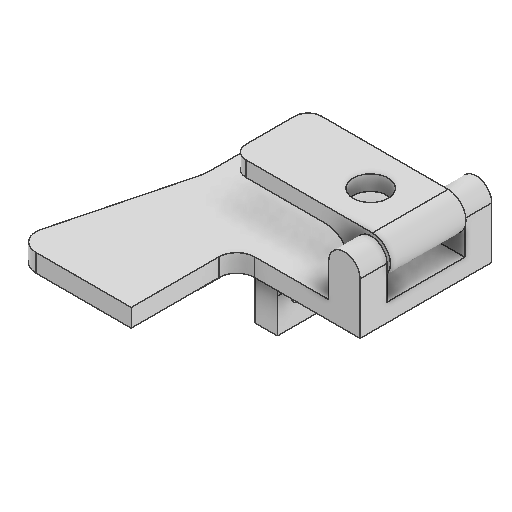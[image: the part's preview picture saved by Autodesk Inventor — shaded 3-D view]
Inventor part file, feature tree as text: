
AUTODESK INVENTOR PART (.ipt)
format: ipt  version: 2025 (Build 290162000, 162)  size: 641,024 bytes
history: native  units: mm
features: projected_geometry x27, sketch x26, extrude x24, fillet x9, plane x7, mirror x3, helix x1
ambient origin geometry x8: Origin, YZ Plane, XZ Plane, XY Plane, X Axis, Y Axis, Z Axis, Center Point
bodies: Solid1 (feature_tree)
feature tree (97):
  extrude  "Extrusion1"  Depth=152.4mm
  plane  "Work Plane1"
  extrude  "Extrusion2"  [1 undecoded]
  extrude  "Extrusion3"  Depth=0.25mm
  extrude  "Extrusion4"  Depth=25.4mm
  fillet  "Fillet1"  Radius=2.75mm
  extrude  "Extrusion5"  Depth=10.0mm TaperAngle=0.0deg
  extrude  "Extrusion6"  Depth=10.0mm
  extrude  "Extrusion7"  Depth=8.0mm TaperAngle=0.0deg
  extrude  "Extrusion8"  Depth=10.0mm TaperAngle=0.0deg
  extrude  "Extrusion9"  Depth=25.4mm TaperAngle=0.0deg
  extrude  "Extrusion10"  Depth=14.0mm
  extrude  "Extrusion11"  Depth=8.0mm
  plane  "Work Plane2"
  extrude  "Extrusion12"  Depth=15.0mm
  mirror  "Mirror1"
  plane  "Work Plane3"
  sketch  "Sketch13"  dims[d37=0.5mm d38=0.5mm]
  plane  "Work Plane4"
  extrude  "Extrusion13"  Depth=0.5mm
  extrude  "Extrusion14"  Depth=0.5mm
  fillet  "Fillet2"  Radius=55.0mm
  fillet  "Fillet3"  [1 undecoded]
  extrude  "Extrusion15"  Depth=10.0mm
  extrude  "Extrusion16"  TaperAngle=0.0deg  [1 undecoded]
  fillet  "Fillet5"  Radius=1.5mm
  extrude  "Extrusion17"  Depth=6.0mm
  extrude  "Extrusion18"  Depth=20.0mm TaperAngle=0.0deg
  fillet  "Fillet6"  Radius=6.0mm
  fillet  "Fillet7"  Radius=6.0mm
  plane  "Work Plane5"
  helix  "Coil2"  [1 undecoded]
  plane  "Work Plane6"
  extrude  "Extrusion19"  Depth=10.0mm
  fillet  "Fillet8"  Radius=2.5mm
  sketch  "Sketch21"  dims[d86=2.0mm d87=0.0mm d88=0.0mm]
  sketch  "Sketch22"  dims[d89=8.0mm d90=0.0mm d91=45.4mm]
  extrude  "Extrusion20"  TaperAngle=0.0deg  [1 undecoded]
  extrude  "Extrusion21"  TaperAngle=0.0deg  [1 undecoded]
  extrude  "Extrusion22"  Depth=45.4mm
  extrude  "Extrusion23"  Depth=10.0mm
  extrude  "Extrusion24"  Depth=50.8mm
  plane  "Work Plane7"
  mirror  "Mirror2"
  fillet  "Fillet9"  Radius=30.0mm
  fillet  "Fillet10"  Radius=2.6mm
  mirror  "Mirror3"
  sketch  "Sketch1"  dims[d0=25.4mm d1=152.4mm]
  sketch  "Sketch2"  dims[d2=10.0mm d3=0.0mm d4=-50.8mm]
  projected_geometry  "Projected Loop1"
  sketch  "Sketch3"  dims[d5=25.4mm d6=0.25mm]
  projected_geometry  "Projected Loop2"
  sketch  "Sketch4"  dims[d7=50.8mm d8=0.0mm d9=25.4mm d10=2.75mm]
  sketch  "Sketch5"  dims[d11=35.45mm d12=0.0mm d13=10.0mm d14=0.0mm]
  projected_geometry  "Projected Loop3"
  sketch  "Sketch6"  dims[d15=10.0mm d16=55.0mm]
  projected_geometry  "Projected Loop4"
  sketch  "Sketch7"  dims[d17=55.0mm d18=8.0mm d19=0.0mm]
  projected_geometry  "Projected Loop5"
  sketch  "Sketch8"  dims[d20=0.0mm d21=0.0mm d22=10.0mm d23=0.0mm]
  projected_geometry  "Projected Loop6"
  sketch  "Sketch9"  dims[d24=25.4mm d25=0.0mm d26=25.4mm d27=0.0mm]
  projected_geometry  "Projected Loop7"
  sketch  "Sketch10"  dims[d28=55.0mm d29=0.0mm d30=14.0mm]
  projected_geometry  "Projected Loop8"
  sketch  "Sketch11"  dims[d31=12.0mm d32=0.0mm d33=8.0mm]
  projected_geometry  "Projected Loop9"
  sketch  "Sketch12"  dims[d34=12.0mm d35=0.0mm d36=15.0mm]
  projected_geometry  "Projected Loop10"
  projected_geometry  "Projected Loop11"
  sketch  "Sketch14"  dims[d39=16.0mm d40=0.5mm d41=55.0mm d42=0.0mm d43=0.0mm d44=0.0mm]
  projected_geometry  "Projected Loop12"
  sketch  "Sketch15"  dims[d45=10.0mm d46=8.0mm]
  projected_geometry  "Projected Loop13"
  sketch  "Sketch16"  dims[d48=12.7mm d49=0.0mm d50=0.0mm d53=1.5mm]
  sketch  "Sketch17"  dims[d54=15.0mm d55=0.0mm d56=6.0mm]
  projected_geometry  "Projected Loop14"
  sketch  "Sketch18"  dims[d57=20.0mm d58=0.0mm d59=20.0mm d60=0.0mm d61=6.0mm d62=6.0mm d71=2.0mm]
  projected_geometry  "Projected Loop15"
  sketch  "Sketch19"  dims[d72=3.0mm d73=10.0mm d74=50.0mm d75=0.0mm d76=90.0deg d77=90.0deg d78=0.0mm d79=0.0mm d80=6.35mm d81=61.0mm d82=2.5mm]
  projected_geometry  "Projected Loop16"
  sketch  "Sketch20"  dims[d83=2.5mm d84=0.0mm d85=0.0mm]
  projected_geometry  "Projected Loop17"
  projected_geometry  "Projected Loop19"
  projected_geometry  "Projected Loop20"
  projected_geometry  "Projected Loop21"
  projected_geometry  "Projected Loop22"
  projected_geometry  "Projected Loop23"
  projected_geometry  "Projected Loop24"
  sketch  "Sketch23"  dims[d92=10.0mm d93=10.0mm]
  projected_geometry  "Projected Loop25"
  sketch  "Sketch24"  dims[d95=25.4mm d96=0.0mm d97=50.8mm d98=30.0mm d99=2.6mm]
  projected_geometry  "Projected Loop26"
  sketch  "Sketch25"  dims[d100=0.0mm d101=0.0mm]
  projected_geometry  "Projected Loop27"
  sketch  "Sketch26"  dims[d102=9.0mm d103=4.0mm d104=0.0mm d105=20.0mm d106=10.0mm]
  projected_geometry  "Projected Loop28"
note: 6 required parameter values undecoded (feature->parameter linkage not recoverable at this tier; creation-order binding heuristic only, values carry confidence <= 0.55)
